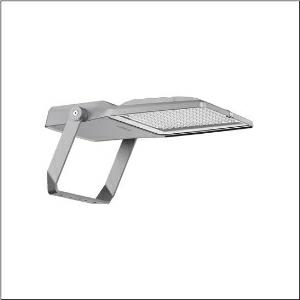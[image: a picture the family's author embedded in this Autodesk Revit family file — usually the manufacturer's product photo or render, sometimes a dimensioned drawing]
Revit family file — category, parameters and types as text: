
# Revit family: floodlight_fl_21_midi___pl64_5xa7786e4e1a_bb08
name_source: partatom
category: Lighting Fixtures
units: mm (PartAtom-declared; Revit-internal decimal feet)

## family parameters
Cut with Voids When Loaded = No
Host = Face
Light Source = No
Part Type = Normal
Room Calculation Point = No
Round Connector Dimension = Use Diameter
Shared = No

## types (1)
- --- (1 x LED, 27140 lm, 212.4 W, 4000K)
    Apparent Load = 212 VA
    CIE Flux Codes = 28 80 98 100 100
    Color Rendering = 70
    Color Temperature = 4000K
    Default Elevation = 1800 mm
    Description = Floodlight FL 21 midi, floodlight, primary light control with lens, of PMMA, primary optical cover: protective disc, of toughened safety glass, transparent, light distribution: PL64, light emission: direct distribution, installation type: surface-mounted, LED, High Power LED, rated luminous flux: 27.140lm, luminous efficacy: 128lm/W, light colour: 740, colour temperature: 4000K, control gear: Smart Interface (Zhaga)D4i, control: overheat protection, constant luminous flux control, time-dependent luminous flux control, flexible luminous flux parameterisation, pre-setting: logarithmic dimming characteristic, with terminal, 6-pole, mains connection: 220..240V, AC, 50/60Hz, start of lifetime: 212W, end of service life: 231W, reduction: 95W, mounting bracket, of diecast aluminium, powder-coated, SITECO metallic grey (DB 702S), corrosivity category C5 mid according to DIN EN ISO 12944, suitable for swimming pools, chlorine-resistant, sealing non-destructively replaceable, mounting bracket, of steel, galvanised, powder-coated, SITECO metallic grey (DB 702S), Smart Interface below and above, protection rating (complete): IP66, insulation class (complete): insulation class II (safety insulation), certification: CE, ENEC, VDE, protection symbol: D, impact resistance: IK08, permissible operating ambient temperature: -40..+40°C, permissible operating ambient temperature for outdoor applications: -40..+50°C, standard: DIN EN 12944, LABS conformity tested according to VDMA 24364:2018-05, packaging unit: 1 piece

Light Distribution: PL64
    Height = 76 mm
    Lamp = 1 x LED
    Lamp Light Flux = 27140 lm
    Lamp Power = 212.4 W
    Lamp count = 1
    Length = 657 mm
    Luminous efficacy = 128 lm/W
    Manufacturer = Siteco
    ModVariant = No
    Model = 5XA7786E4E1A
    Number of Poles = 1
    OnlyDefault = Yes
    Power Factor = 1
    Product Name = Floodlight FL 21 midi | PL64
    Product group = floodlight | pylon annexe
    ProductGroupID = 6201
    Protection Class = Protection class II
    Protection Degree = IP 66
    RLX_Detail_Level = 1
    RLX_Emergency_Light_Flux = 0 lm
    RLX_Emergency_Type = 0
    RLX_Emergency_Type_DB = No
    RlxData = <blob elided: 101653 chars, md5=387f2c25>
    Socket = socket
    Standby Power = 0 W
    System Light Flux = 27140 lm
    System Power = 212 W
    Type Comments = factory setting: luminous flux: 100 % | dim-lin: 254 | 710 mA
    Type Image = l_1006876.jpg
    URL = http://relux.com
    VarID = @adj_093339
    Voltage = 0 V
    Weight = 0.00 kg
    Width = 442 mm

## geometry (parser evidence)
native form markers: Blend x4, Sweep x12
no freeform markers — native parametric forms only
